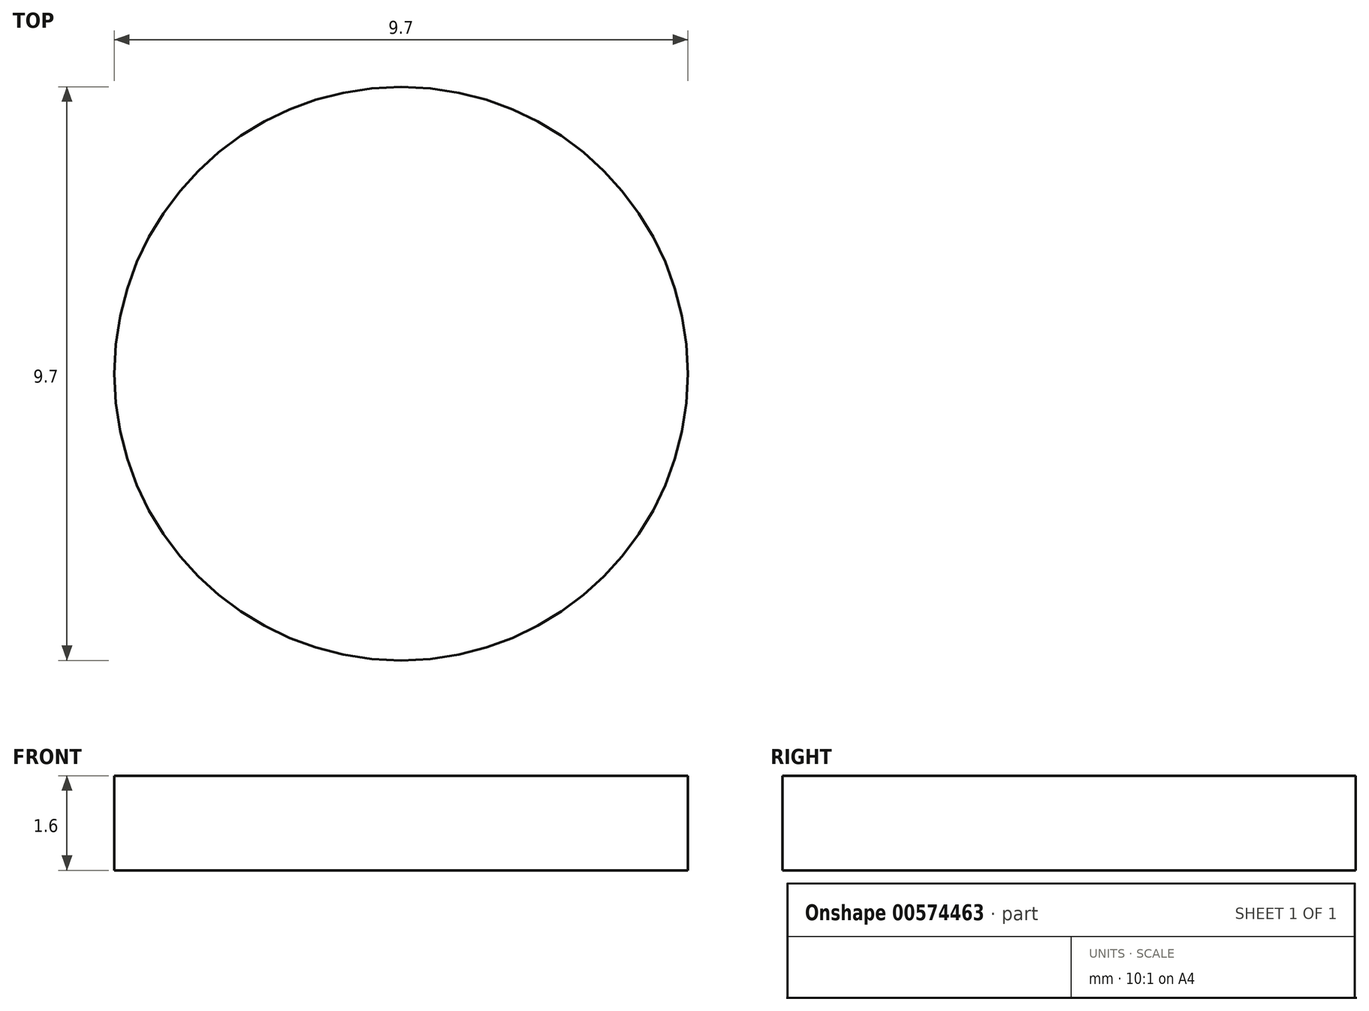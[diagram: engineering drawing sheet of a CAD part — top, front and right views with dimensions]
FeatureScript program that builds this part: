
annotation { "Feature Type Name" : "Feature", "Feature Type Description" : "" }
export const myFeature = defineFeature(function(context is Context, id is Id, definition is map)
    precondition{}
    {
        {
            var Q0;
            Q0=qCreatedBy(makeId("Top.planeOp"),FACE);
            var sketch = newSketch(context, id + "F0", { "sketchPlane" : qUnion([Q0])});
            skCircle(sketch, "E0", {"center": v(0, 0) * mm, "radius": 4.85 * mm});
            skSolve(sketch);
        }
        {
            var Q0;
            Q0=makeQuery(id+"F0.imprint","IMPRINT",FACE,{"disambiguationData":[TD([[makeQuery(id+"F0.imprint","IMPRINT",EDGE,{"derivedFrom":sQuery(id+"F0.wireOp",EDGE,"E0")}),1.0]])]});
            extrude(context, id + "F1", {"entities" : qUnion([Q0]), "depth" : 1.6 * mm, "offsetDistance" : 25 * mm});
        }
    });
